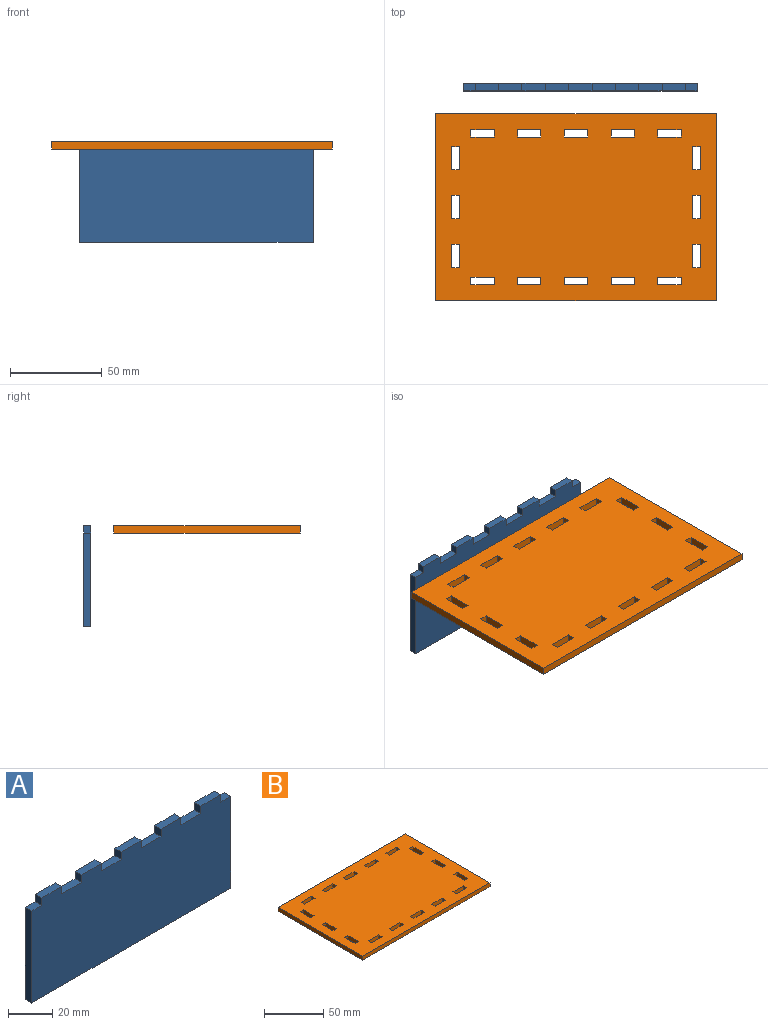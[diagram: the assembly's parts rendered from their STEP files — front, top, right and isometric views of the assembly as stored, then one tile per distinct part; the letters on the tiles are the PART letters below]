
ASSEMBLY  parts=2 mates=1
PART A: 26 faces, bbox 127x4.1x54.9 mm
  f0: plane 4.06x4.06mm, normal (1,0,0), area 16.5mm2, adj f1,f23,f24,f25
  f1: plane 12.7x4.06mm, normal (0,0,1), area 51.6mm2, adj f0,f2,f24,f25
  f2: plane 4.06x4.06mm, normal (-1,0,0), area 16.5mm2, adj f1,f3,f24,f25
  f3: plane 12.7x4.06mm, normal (0,0,1), area 51.6mm2, adj f2,f4,f24,f25
  f4: plane 4.06x4.06mm, normal (1,0,0), area 16.5mm2, adj f3,f5,f24,f25
  f5: plane 12.7x4.06mm, normal (0,0,1), area 51.6mm2, adj f4,f6,f24,f25
  f6: plane 4.06x4.06mm, normal (-1,0,0), area 16.5mm2, adj f5,f7,f24,f25
  f7: plane 12.7x4.06mm, normal (0,0,1), area 51.6mm2, adj f6,f8,f24,f25
  f8: plane 4.06x4.06mm, normal (1,0,0), area 16.5mm2, adj f7,f9,f24,f25
  f9: plane 12.7x4.06mm, normal (0,0,1), area 51.6mm2, adj f8,f10,f24,f25
  f10: plane 4.06x4.06mm, normal (-1,0,0), area 16.5mm2, adj f9,f11,f24,f25
  f11: plane 12.7x4.06mm, normal (0,0,1), area 51.6mm2, adj f10,f12,f24,f25
  f12: plane 4.06x4.06mm, normal (1,0,0), area 16.5mm2, adj f11,f13,f24,f25
  f13: plane 12.7x4.06mm, normal (0,0,1), area 51.6mm2, adj f12,f14,f24,f25
  f14: plane 4.06x4.06mm, normal (-1,0,0), area 16.5mm2, adj f13,f15,f24,f25
  f15: plane 12.7x4.06mm, normal (0,0,1), area 51.6mm2, adj f14,f16,f24,f25
  f16: plane 4.06x4.06mm, normal (1,0,0), area 16.5mm2, adj f15,f17,f24,f25
  f17: plane 6.35x4.06mm, normal (0,0,1), area 25.8mm2, adj f16,f18,f24,f25
  f18: plane 50.8x4.06mm, normal (1,0,0), area 206.5mm2, adj f17,f19,f24,f25
  f19: plane 127x4.06mm, normal (0,0,-1), area 516.1mm2, adj f18,f20,f24,f25
  f20: plane 50.8x4.06mm, normal (-1,0,0), area 206.5mm2, adj f19,f21,f24,f25
  f21: plane 6.35x4.06mm, normal (0,0,1), area 25.8mm2, adj f20,f22,f24,f25
  f22: plane 4.06x4.06mm, normal (-1,0,0), area 16.5mm2, adj f21,f23,f24,f25
  f23: plane 12.7x4.06mm, normal (0,0,1), area 51.6mm2, adj f0,f22,f24,f25
  f24: plane 127x54.86mm, normal (0,1,0), area 6709.7mm2, adj f0,f1,f2,f3,f4,f5,f6,f7
  f25: plane 127x54.86mm, normal (0,-1,0), area 6709.7mm2, adj f0,f1,f2,f3,f4,f5,f6,f7
PART B: 70 faces, bbox 152.4x101.6x4.1 mm
  f0: plane 12.7x4.06mm, normal (-1,0,0), area 51.6mm2, adj f1,f67,f68,f69
  f1: plane 4.06x4.06mm, normal (0,1,0), area 16.5mm2, adj f0,f2,f68,f69
  f2: plane 12.7x4.06mm, normal (1,0,0), area 51.6mm2, adj f1,f67,f68,f69
  f3: plane 12.7x4.06mm, normal (0,1,0), area 51.6mm2, adj f4,f51,f68,f69
  f4: plane 4.06x4.06mm, normal (1,0,0), area 16.5mm2, adj f3,f5,f68,f69
  f5: plane 12.7x4.06mm, normal (0,-1,0), area 51.6mm2, adj f4,f51,f68,f69
  f6: plane 101.6x4.06mm, normal (-1,0,0), area 412.9mm2, adj f7,f52,f68,f69
  f7: plane 152.4x4.06mm, normal (0,-1,0), area 619.4mm2, adj f6,f8,f68,f69
  f8: plane 101.6x4.06mm, normal (1,0,0), area 412.9mm2, adj f7,f52,f68,f69
  f9: plane 12.7x4.06mm, normal (0,1,0), area 51.6mm2, adj f10,f53,f68,f69
  f10: plane 4.06x4.06mm, normal (1,0,0), area 16.5mm2, adj f9,f11,f68,f69
  f11: plane 12.7x4.06mm, normal (0,-1,0), area 51.6mm2, adj f10,f53,f68,f69
  f12: plane 4.06x4.06mm, normal (1,0,0), area 16.5mm2, adj f13,f54,f68,f69
  f13: plane 12.7x4.06mm, normal (0,-1,0), area 51.6mm2, adj f12,f14,f68,f69
  f14: plane 4.06x4.06mm, normal (-1,0,0), area 16.5mm2, adj f13,f54,f68,f69
  f15: plane 4.06x4.06mm, normal (1,0,0), area 16.5mm2, adj f16,f55,f68,f69
  f16: plane 12.7x4.06mm, normal (0,-1,0), area 51.6mm2, adj f15,f17,f68,f69
  f17: plane 4.06x4.06mm, normal (-1,0,0), area 16.5mm2, adj f16,f55,f68,f69
  f18: plane 4.06x4.06mm, normal (1,0,0), area 16.5mm2, adj f19,f56,f68,f69
  f19: plane 12.7x4.06mm, normal (0,-1,0), area 51.6mm2, adj f18,f20,f68,f69
  f20: plane 4.06x4.06mm, normal (-1,0,0), area 16.5mm2, adj f19,f56,f68,f69
  f21: plane 4.06x4.06mm, normal (1,0,0), area 16.5mm2, adj f22,f57,f68,f69
  f22: plane 12.7x4.06mm, normal (0,-1,0), area 51.6mm2, adj f21,f23,f68,f69
  f23: plane 4.06x4.06mm, normal (-1,0,0), area 16.5mm2, adj f22,f57,f68,f69
  f24: plane 12.7x4.06mm, normal (0,1,0), area 51.6mm2, adj f25,f58,f68,f69
  f25: plane 4.06x4.06mm, normal (1,0,0), area 16.5mm2, adj f24,f26,f68,f69
  f26: plane 12.7x4.06mm, normal (0,-1,0), area 51.6mm2, adj f25,f58,f68,f69
  f27: plane 4.06x4.06mm, normal (-1,0,0), area 16.5mm2, adj f28,f59,f68,f69
  f28: plane 12.7x4.06mm, normal (0,1,0), area 51.6mm2, adj f27,f29,f68,f69
  f29: plane 4.06x4.06mm, normal (1,0,0), area 16.5mm2, adj f28,f59,f68,f69
  f30: plane 12.7x4.06mm, normal (0,1,0), area 51.6mm2, adj f31,f60,f68,f69
  f31: plane 4.06x4.06mm, normal (1,0,0), area 16.5mm2, adj f30,f32,f68,f69
  f32: plane 12.7x4.06mm, normal (0,-1,0), area 51.6mm2, adj f31,f60,f68,f69
  f33: plane 4.06x4.06mm, normal (-1,0,0), area 16.5mm2, adj f34,f61,f68,f69
  f34: plane 12.7x4.06mm, normal (0,1,0), area 51.6mm2, adj f33,f35,f68,f69
  f35: plane 4.06x4.06mm, normal (1,0,0), area 16.5mm2, adj f34,f61,f68,f69
  f36: plane 4.06x4.06mm, normal (0,1,0), area 16.5mm2, adj f37,f62,f68,f69
  f37: plane 12.7x4.06mm, normal (1,0,0), area 51.6mm2, adj f36,f38,f68,f69
  f38: plane 4.06x4.06mm, normal (0,-1,0), area 16.5mm2, adj f37,f62,f68,f69
  f39: plane 12.7x4.06mm, normal (1,0,0), area 51.6mm2, adj f40,f63,f68,f69
  f40: plane 4.06x4.06mm, normal (0,-1,0), area 16.5mm2, adj f39,f41,f68,f69
  f41: plane 12.7x4.06mm, normal (-1,0,0), area 51.6mm2, adj f40,f63,f68,f69
  f42: plane 12.7x4.06mm, normal (1,0,0), area 51.6mm2, adj f43,f64,f68,f69
  f43: plane 4.06x4.06mm, normal (0,-1,0), area 16.5mm2, adj f42,f44,f68,f69
  f44: plane 12.7x4.06mm, normal (-1,0,0), area 51.6mm2, adj f43,f64,f68,f69
  f45: plane 12.7x4.06mm, normal (1,0,0), area 51.6mm2, adj f46,f65,f68,f69
  f46: plane 4.06x4.06mm, normal (0,-1,0), area 16.5mm2, adj f45,f47,f68,f69
  f47: plane 12.7x4.06mm, normal (-1,0,0), area 51.6mm2, adj f46,f65,f68,f69
  f48: plane 12.7x4.06mm, normal (1,0,0), area 51.6mm2, adj f49,f66,f68,f69
  f49: plane 4.06x4.06mm, normal (0,-1,0), area 16.5mm2, adj f48,f50,f68,f69
  f50: plane 12.7x4.06mm, normal (-1,0,0), area 51.6mm2, adj f49,f66,f68,f69
  f51: plane 4.06x4.06mm, normal (-1,0,0), area 16.5mm2, adj f3,f5,f68,f69
  f52: plane 152.4x4.06mm, normal (0,1,0), area 619.4mm2, adj f6,f8,f68,f69
  f53: plane 4.06x4.06mm, normal (-1,0,0), area 16.5mm2, adj f9,f11,f68,f69
  f54: plane 12.7x4.06mm, normal (0,1,0), area 51.6mm2, adj f12,f14,f68,f69
  f55: plane 12.7x4.06mm, normal (0,1,0), area 51.6mm2, adj f15,f17,f68,f69
  f56: plane 12.7x4.06mm, normal (0,1,0), area 51.6mm2, adj f18,f20,f68,f69
  f57: plane 12.7x4.06mm, normal (0,1,0), area 51.6mm2, adj f21,f23,f68,f69
  f58: plane 4.06x4.06mm, normal (-1,0,0), area 16.5mm2, adj f24,f26,f68,f69
  f59: plane 12.7x4.06mm, normal (0,-1,0), area 51.6mm2, adj f27,f29,f68,f69
  f60: plane 4.06x4.06mm, normal (-1,0,0), area 16.5mm2, adj f30,f32,f68,f69
  f61: plane 12.7x4.06mm, normal (0,-1,0), area 51.6mm2, adj f33,f35,f68,f69
  f62: plane 12.7x4.06mm, normal (-1,0,0), area 51.6mm2, adj f36,f38,f68,f69
  f63: plane 4.06x4.06mm, normal (0,1,0), area 16.5mm2, adj f39,f41,f68,f69
  f64: plane 4.06x4.06mm, normal (0,1,0), area 16.5mm2, adj f42,f44,f68,f69
  f65: plane 4.06x4.06mm, normal (0,1,0), area 16.5mm2, adj f45,f47,f68,f69
  f66: plane 4.06x4.06mm, normal (0,1,0), area 16.5mm2, adj f48,f50,f68,f69
  f67: plane 4.06x4.06mm, normal (0,-1,0), area 16.5mm2, adj f0,f2,f68,f69
  f68: plane 152.4x101.6mm, normal (0,0,1), area 14658mm2, adj f0,f1,f2,f3,f4,f5,f6,f7
  f69: plane 152.4x101.6mm, normal (0,0,-1), area 14658mm2, adj f0,f1,f2,f3,f4,f5,f6,f7
PLACE A t=(-30.87,47.17,15.68)mm
PLACE B rot(axis=(1,0,0),180deg) t=(-33.31,-79.49,19.74)mm
MATE planar B.f68 <-> A.f9  axis (0,0,-1) through (42.89,-28.69,15.68)mm
